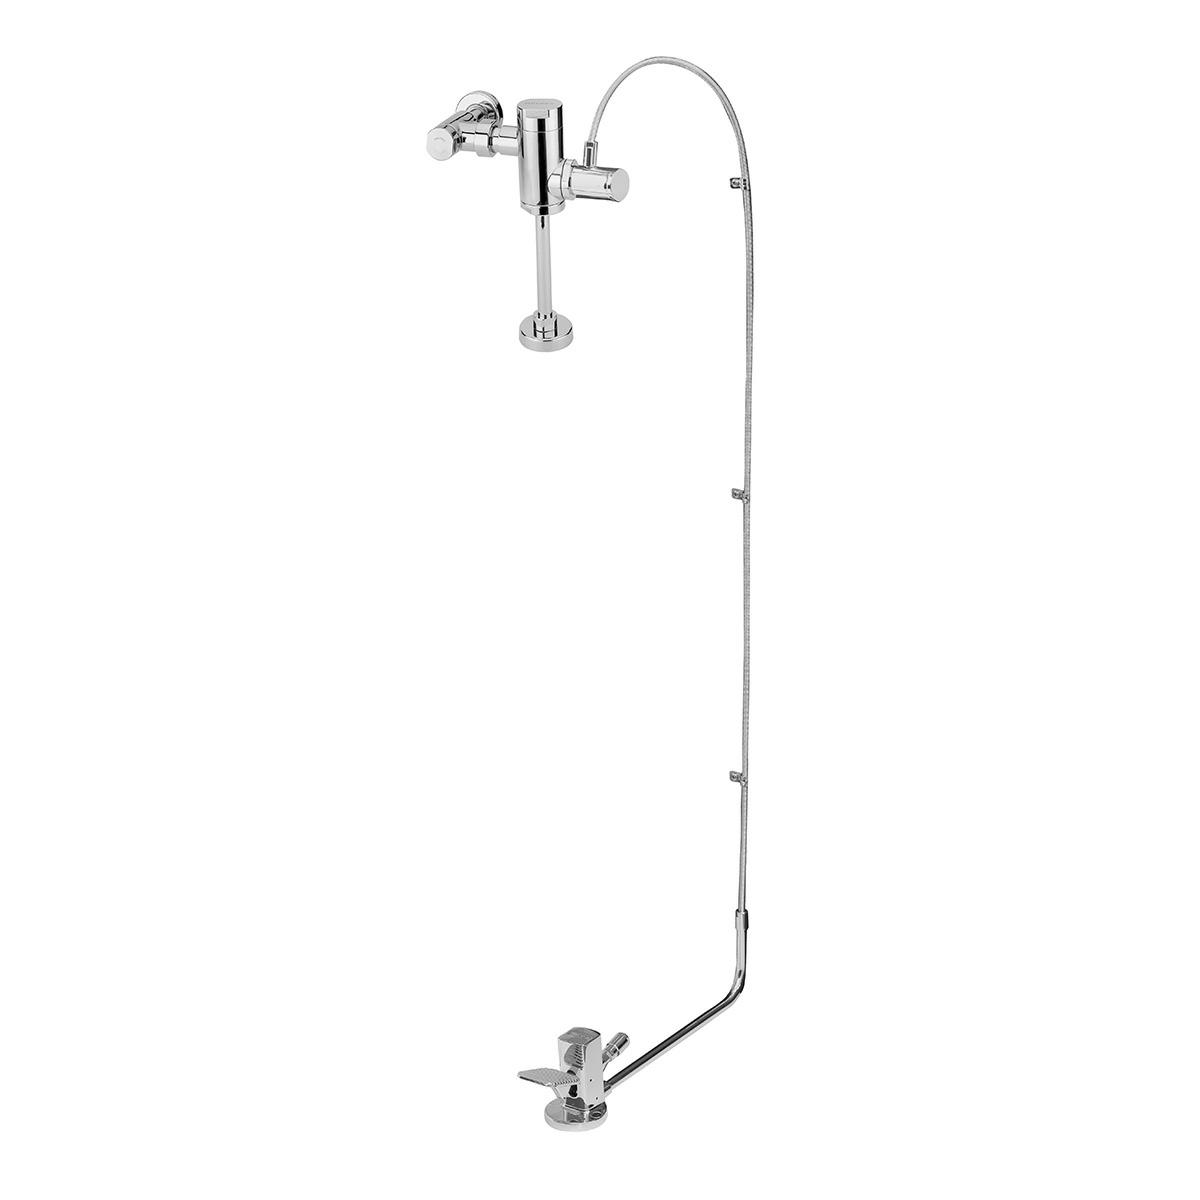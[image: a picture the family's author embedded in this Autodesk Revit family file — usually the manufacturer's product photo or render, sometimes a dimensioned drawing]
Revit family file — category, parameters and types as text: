
# Revit family: 313-19
name_source: partatom
category: Aparatos sanitarios
units: mm (PartAtom-declared; Revit-internal decimal feet)

## family parameters
Compartido = Sí
Corte con vacíos al cargar = No
Cota de conector redondo = Diámetro de uso
Número OmniClass = 23.45.00.00
Punto de cálculo de habitación = No
Se basa en plano de trabajo = No
Siempre vertical = Sí
Tipo de pieza = Normal
Título OmniClass = Sanitary, Laundry, and Cleaning Equipment

## types (1)
- 185-19
    Chrome = Brass Chromed
    Comentarios de tipo = Flush Valves
    Conexión AF = Sí
    Connection = Conexión de alimentación: tubo 25,4 mm
    Descripción = Fluxómetro de pedal expuesto para mingitorio 3LPD
    Documentation = https://www.helvex.com.mx
    Elevación por defecto = 0"
    Fabricante = HELVEX
    Flow = 2 - 3 Lts Per Flush
    Imagen de tipo = 313-19.jpg
    Instructive = https://www.helvex.com.mx
    Max. Working Pressure = 85.3 psi
    Min. Working Pressure = 14.2 psi
    Modelo = 313-19
    Note = Fluxómetro de pedal expuesto para mingitorio de 19mm a 3LPD.
    URL = https://www.helvex.com.mx

## geometry (parser evidence)
native form markers: Sweep x3
no freeform markers — native parametric forms only
